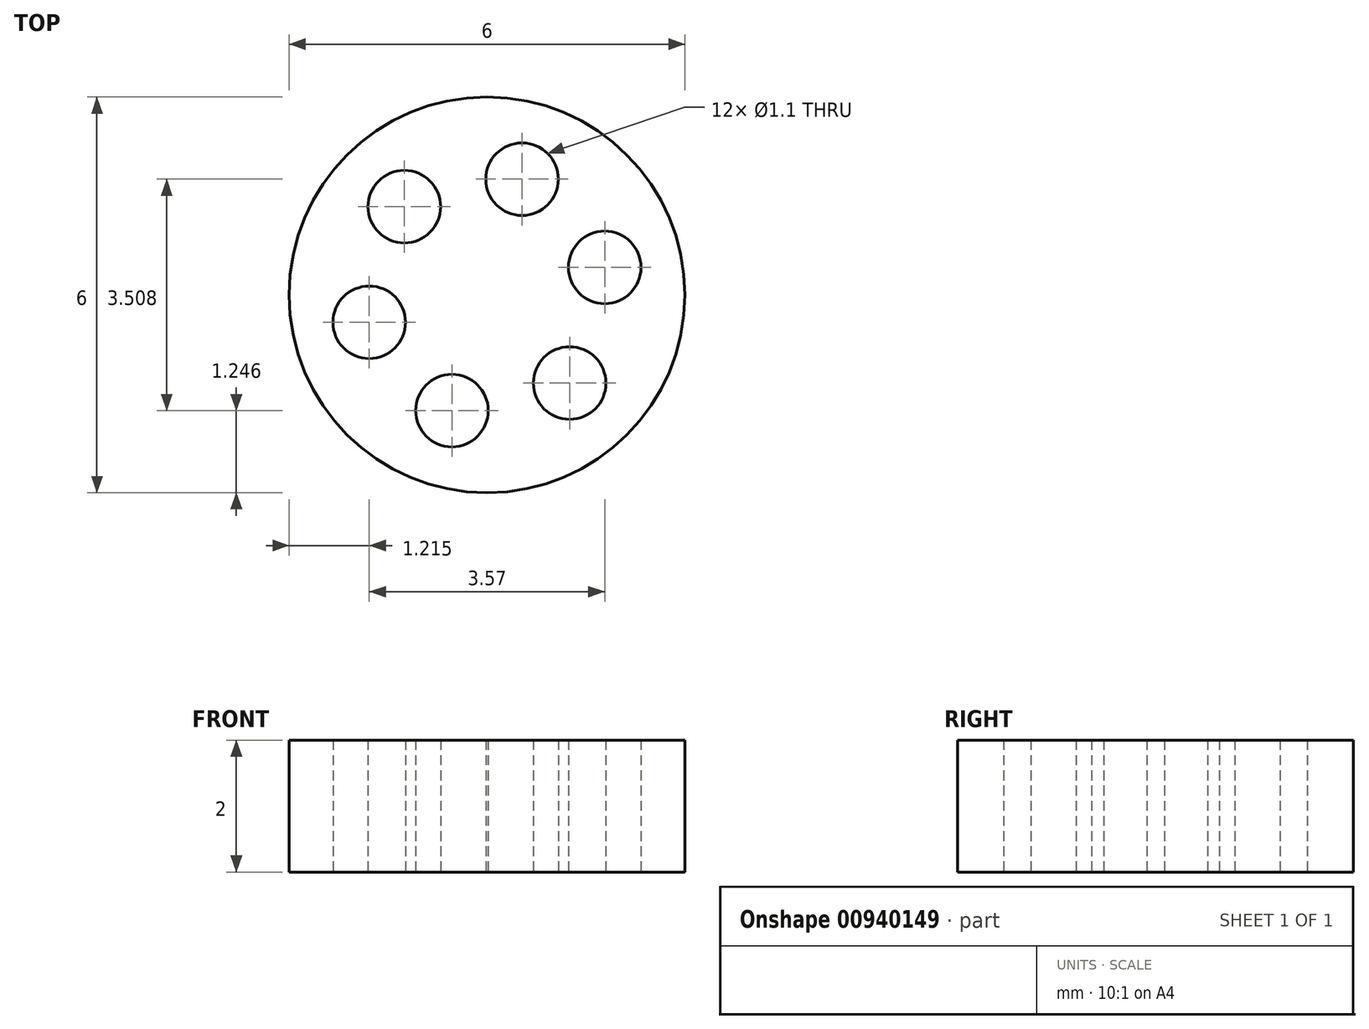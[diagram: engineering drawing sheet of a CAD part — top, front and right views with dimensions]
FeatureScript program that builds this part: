
annotation { "Feature Type Name" : "Feature", "Feature Type Description" : "" }
export const myFeature = defineFeature(function(context is Context, id is Id, definition is map)
    precondition{}
    {
        {
            var Q0;
            Q0=qCreatedBy(makeId("Top.planeOp"),FACE);
            var sketch = newSketch(context, id + "F0", { "sketchPlane" : qUnion([Q0])});
            skCircle(sketch, "E0", {"center": v(0, 0) * mm, "radius": 3 * mm});
            skSolve(sketch);
        }
        {
            var Q0;
            Q0=qCreatedBy(makeId("Top.planeOp"),FACE);
            var sketch = newSketch(context, id + "F1", { "sketchPlane" : qUnion([Q0])});
            skCircle(sketch, "E1", {"center": v(-1.25, 1.34) * mm, "radius": 0.55 * mm});
            skCircle(sketch, "E2.1.0", {"center": v(-1.79, -0.42) * mm, "radius": 0.55 * mm});
            skCircle(sketch, "E2.2.0", {"center": v(-0.53, -1.75) * mm, "radius": 0.55 * mm});
            skCircle(sketch, "E2.3.0", {"center": v(1.25, -1.34) * mm, "radius": 0.55 * mm});
            skCircle(sketch, "E2.4.0", {"center": v(1.79, 0.42) * mm, "radius": 0.55 * mm});
            skCircle(sketch, "E2.5.0", {"center": v(0.53, 1.75) * mm, "radius": 0.55 * mm});
            skPoint(sketch, "E2.center", {"position": v(0, 0) * mm});
            skSolve(sketch);
        }
        {
            var Q0;
            Q0 = qSketchRegion(id + "F0", true);
            extrude(context, id + "F2", {"entities" : qUnion([Q0]), "depth" : 2 * mm, "offsetDistance" : 25 * mm});
        }
        {
            var Q0;
            Q0 = qSketchRegion(id + "F1", true);
            extrude(context, id + "F3", {"entities" : qUnion([Q0]), "operationType" : NewBodyOperationType.REMOVE, "depth" : 2 * mm, "offsetDistance" : 25 * mm});
        }
    });
